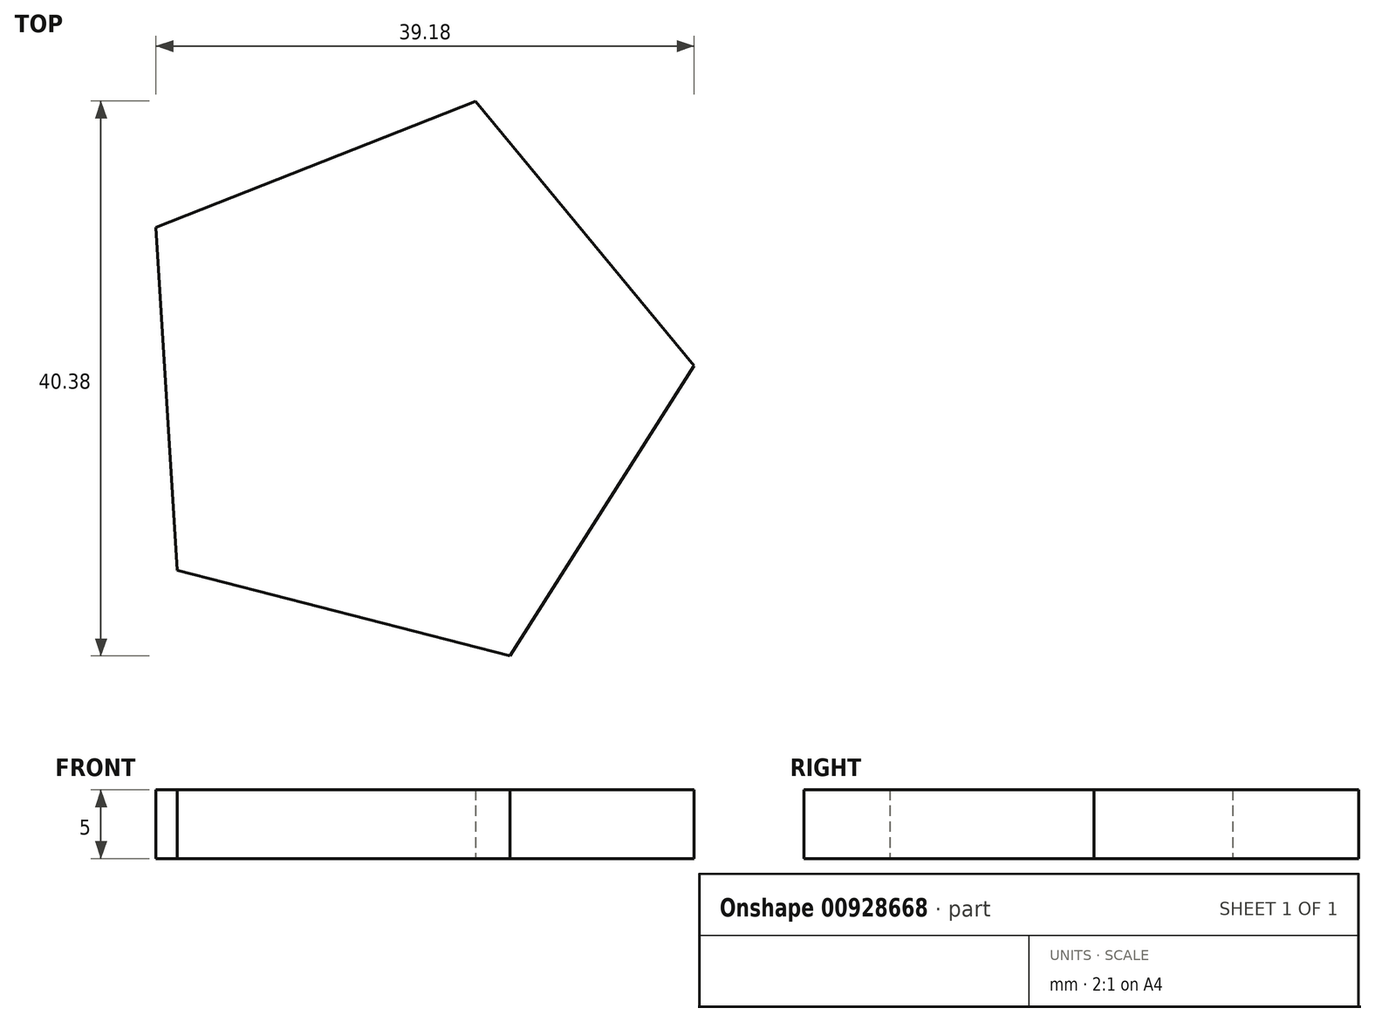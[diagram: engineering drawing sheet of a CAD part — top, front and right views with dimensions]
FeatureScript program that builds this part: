
annotation { "Feature Type Name" : "Feature", "Feature Type Description" : "" }
export const myFeature = defineFeature(function(context is Context, id is Id, definition is map)
    precondition{}
    {
        {
            var Q0;
            Q0=qCreatedBy(makeId("Top.planeOp"),FACE);
            var sketch = newSketch(context, id + "F0", { "sketchPlane" : qUnion([Q0])});
            skCircle(sketch, "E0.cCircle", {"center": v(0, 0) * mm, "radius": 21.27 * mm, "construction": true});
            skLineSegment(sketch, "E0.0", {"start": v(7.82, -19.78) * mm, "end": v(-16.4, -13.55) * mm});
            skLineSegment(sketch, "E0.1", {"start": v(-16.4, -13.55) * mm, "end": v(-17.95, 11.4) * mm});
            skLineSegment(sketch, "E0.2", {"start": v(-17.95, 11.4) * mm, "end": v(5.3, 20.6) * mm});
            skLineSegment(sketch, "E0.3", {"start": v(5.3, 20.6) * mm, "end": v(21.23, 1.32) * mm});
            skLineSegment(sketch, "E0.4", {"start": v(21.23, 1.32) * mm, "end": v(7.82, -19.78) * mm});
            skSolve(sketch);
        }
        {
            var Q0;
            Q0=makeQuery(id+"F0.imprint","IMPRINT",FACE,{"disambiguationData":[TD([[makeQuery(id+"F0.imprint","IMPRINT",EDGE,{"derivedFrom":sQuery(id+"F0.wireOp",EDGE,"E0.0")}),-1.0]])]});
            extrude(context, id + "F1", {"entities" : qUnion([Q0]), "depth" : 5 * mm, "offsetDistance" : 25 * mm});
        }
    });
